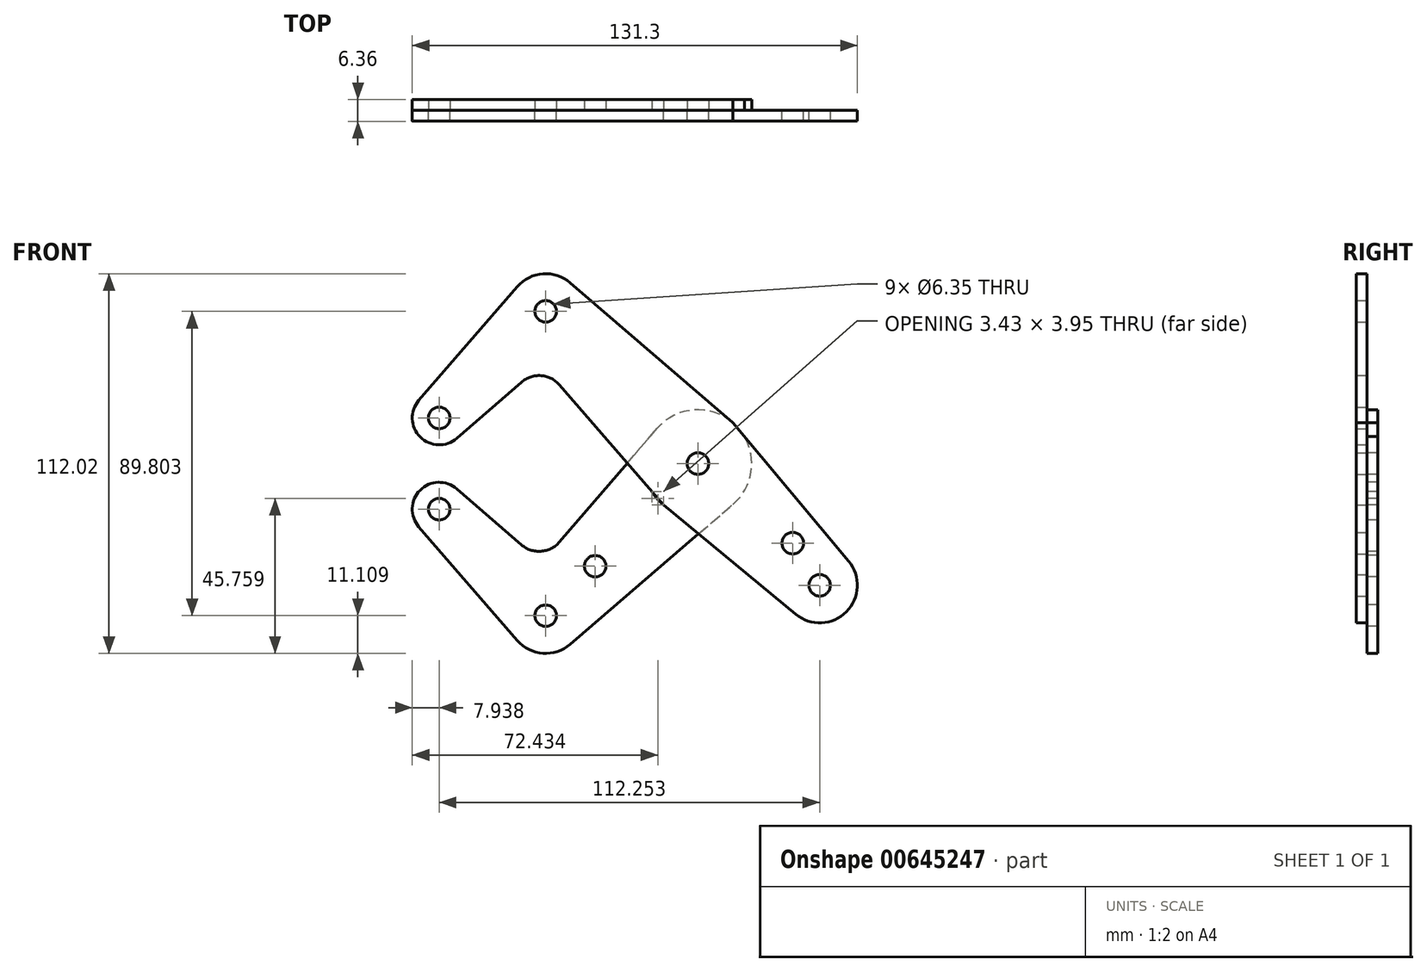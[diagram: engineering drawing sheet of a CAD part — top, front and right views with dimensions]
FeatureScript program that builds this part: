
annotation { "Feature Type Name" : "Feature", "Feature Type Description" : "" }
export const myFeature = defineFeature(function(context is Context, id is Id, definition is map)
    precondition{}
    {
        {
            var Q0;
            Q0=qCreatedBy(makeId("Front.planeOp"),FACE);
            var sketch = newSketch(context, id + "F0", { "sketchPlane" : qUnion([Q0])});
            skLineSegment(sketch, "E0", {"start": v(-76.33, 13.47) * mm, "end": v(-44.9, 44.9) * mm, "construction": true});
            skLineSegment(sketch, "E1", {"start": v(-44.9, 44.9) * mm, "end": v(35.92, -35.92) * mm, "construction": true});
            skCircle(sketch, "E2", {"center": v(-76.33, 13.47) * mm, "radius": 3.18 * mm});
            skCircle(sketch, "E3", {"center": v(-76.33, 13.47) * mm, "radius": 7.94 * mm});
            skCircle(sketch, "E4", {"center": v(-44.9, 44.9) * mm, "radius": 11.11 * mm});
            skCircle(sketch, "E5", {"center": v(-44.9, 44.9) * mm, "radius": 3.18 * mm});
            skPoint(sketch, "E6", {"position": v(0, 0) * mm});
            skCircle(sketch, "E7", {"center": v(0, 0) * mm, "radius": 3.98 * mm});
            skCircle(sketch, "E8", {"center": v(0, 0) * mm, "radius": 3.18 * mm});
            skCircle(sketch, "E9", {"center": v(0, 0) * mm, "radius": 15.88 * mm});
            skCircle(sketch, "E10", {"center": v(35.92, -35.92) * mm, "radius": 3.18 * mm});
            skCircle(sketch, "E11", {"center": v(35.92, -35.92) * mm, "radius": 11.11 * mm});
            skCircle(sketch, "E12", {"center": v(27.97, -23.48) * mm, "radius": 3.18 * mm});
            skLineSegment(sketch, "E13", {"start": v(-82.33, 18.67) * mm, "end": v(-53.3, 52.18) * mm});
            skLineSegment(sketch, "E14", {"start": v(-37.66, 53.33) * mm, "end": v(10.35, 12.04) * mm});
            skLineSegment(sketch, "E15", {"start": v(44.45, -28.8) * mm, "end": v(10.35, 12.04) * mm});
            skLineSegment(sketch, "E16", {"start": v(28.83, -44.48) * mm, "end": v(-10.12, -12.23) * mm});
            skLineSegment(sketch, "E17", {"start": v(-71.13, 7.47) * mm, "end": v(-52.03, 24.02) * mm});
            skLineSegment(sketch, "E18", {"start": v(-10.12, -12.23) * mm, "end": v(-40.82, 23.21) * mm});
            skArc(sketch, "E19.filletArc", {"start": v(-40.82, 23.21) * mm, "mid": v(-46.26, 25.94) * mm, "end": v(-52.03, 24.02) * mm});
            skLineSegment(sketch, "E20", {"start": v(0, 0) * mm, "end": v(-44.9, -44.9) * mm, "construction": true});
            skLineSegment(sketch, "E21", {"start": v(-44.9, -44.9) * mm, "end": v(-76.33, -13.47) * mm, "construction": true});
            skCircle(sketch, "E22", {"center": v(-76.33, -13.47) * mm, "radius": 7.94 * mm});
            skCircle(sketch, "E23", {"center": v(-76.33, -13.47) * mm, "radius": 3.18 * mm});
            skCircle(sketch, "E24", {"center": v(-44.9, -44.9) * mm, "radius": 11.11 * mm});
            skCircle(sketch, "E25", {"center": v(-44.9, -44.9) * mm, "radius": 3.18 * mm});
            skCircle(sketch, "E26", {"center": v(-30.3, -30.3) * mm, "radius": 3.18 * mm});
            skLineSegment(sketch, "E27", {"start": v(-71.13, -7.47) * mm, "end": v(-52.08, -23.98) * mm});
            skLineSegment(sketch, "E28", {"start": v(-82.33, -18.67) * mm, "end": v(-53.3, -52.18) * mm});
            skLineSegment(sketch, "E29", {"start": v(-40.85, -23.15) * mm, "end": v(-11.26, 11.26) * mm});
            skLineSegment(sketch, "E30", {"start": v(-37.66, -53.33) * mm, "end": v(11.26, -11.26) * mm});
            skArc(sketch, "E31.filletArc", {"start": v(-52.08, -23.98) * mm, "mid": v(-46.3, -25.9) * mm, "end": v(-40.85, -23.15) * mm});
            skSolve(sketch);
        }
        {
            var Q0;
            Q0=makeQuery(id+"F0.imprint","IMPRINT",FACE,{"disambiguationData":[TD([[makeQuery(id+"F0.imprint","IMPRINT",EDGE,{"derivedFrom":sQuery(id+"F0.wireOp",EDGE,"E2")}),-1.0]])]});
            var Q1;
            {var subQ0=sQuery(id+"F0.wireOp",EDGE,"E13");Q1=makeQuery(id+"F0.imprint","IMPRINT",FACE,{"disambiguationData":[TD([[makeQuery(id+"F0.imprint","IMPRINT",EDGE,{"derivedFrom":subQ0}),-1.0]])]});}
            var Q2;
            Q2=makeQuery(id+"F0.imprint","IMPRINT",FACE,{"disambiguationData":[TD([[makeQuery(id+"F0.imprint","IMPRINT",EDGE,{"derivedFrom":sQuery(id+"F0.wireOp",EDGE,"E5")}),-1.0]])]});
            var Q3;
            Q3=makeQuery(id+"F0.imprint","IMPRINT",FACE,{"disambiguationData":[TD([[makeQuery(id+"F0.imprint","IMPRINT",EDGE,{"derivedFrom":sQuery(id+"F0.wireOp",EDGE,"E7")}),-1.0]])]});
            var Q4;
            Q4=makeQuery(id+"F0.imprint","IMPRINT",FACE,{"disambiguationData":[TD([[makeQuery(id+"F0.imprint","IMPRINT",EDGE,{"derivedFrom":sQuery(id+"F0.wireOp",EDGE,"E12")}),-1.0]])]});
            var Q5;
            Q5=makeQuery(id+"F0.imprint","IMPRINT",FACE,{"disambiguationData":[TD([[makeQuery(id+"F0.imprint","IMPRINT",EDGE,{"derivedFrom":sQuery(id+"F0.wireOp",EDGE,"E10")}),-1.0]])]});
            var Q6;
            Q6=makeQuery(id+"F0.imprint","IMPRINT",FACE,{"disambiguationData":[TD([[makeQuery(id+"F0.imprint","IMPRINT",EDGE,{"derivedFrom":sQuery(id+"F0.wireOp",EDGE,"E7")}),1.0]])]});
            var Q7;
            {var subQ0=sQuery(id+"F0.wireOp",EDGE,"E29");var subQ1=sQuery(id+"F0.wireOp",EDGE,"E9");var subQ2=makeQuery(id+"F0.imprint","INTERSECT",VERTEX,{"derivedFrom":[subQ1,subQ0]});Q7=makeQuery(id+"F0.imprint","IMPRINT",FACE,{"disambiguationData":[TD([[makeQuery(id+"F0.imprint","IMPRINT",EDGE,{"disambiguationData":[TD([[subQ2,-1.0]])],"derivedFrom":subQ1}),-1.0]])]});}
            var Q8;
            {var subQ1=sQuery(id+"F0.wireOp",EDGE,"E9");var subQ3=sQuery(id+"F0.wireOp",EDGE,"E30");var subQ4=makeQuery(id+"F0.imprint","INTERSECT",VERTEX,{"derivedFrom":[subQ1,subQ3]});Q8=makeQuery(id+"F0.imprint","IMPRINT",FACE,{"disambiguationData":[TD([[makeQuery(id+"F0.imprint","IMPRINT",EDGE,{"disambiguationData":[TD([[subQ4,1.0]])],"derivedFrom":subQ3}),1.0]])]});}
            extrude(context, id + "F1", {"entities" : qUnion([Q0, Q1, Q2, Q3, Q4, Q5, Q6, Q7, Q8]), "depth" : 3.17 * mm, "offsetDistance" : 25.4 * mm});
        }
        {
            var Q0;
            Q0=makeQuery(id+"F0.imprint","IMPRINT",FACE,{"disambiguationData":[TD([[makeQuery(id+"F0.imprint","IMPRINT",EDGE,{"derivedFrom":sQuery(id+"F0.wireOp",EDGE,"E23")}),-1.0]])]});
            var Q1;
            Q1=makeQuery(id+"F0.imprint","IMPRINT",FACE,{"disambiguationData":[TD([[makeQuery(id+"F0.imprint","IMPRINT",EDGE,{"derivedFrom":sQuery(id+"F0.wireOp",EDGE,"E26")}),-1.0]])]});
            var Q2;
            Q2=makeQuery(id+"F0.imprint","IMPRINT",FACE,{"disambiguationData":[TD([[makeQuery(id+"F0.imprint","IMPRINT",EDGE,{"derivedFrom":sQuery(id+"F0.wireOp",EDGE,"E25")}),-1.0]])]});
            var Q3;
            {var subQ0=sQuery(id+"F0.wireOp",EDGE,"E29");var subQ1=sQuery(id+"F0.wireOp",EDGE,"E9");var subQ2=makeQuery(id+"F0.imprint","INTERSECT",VERTEX,{"derivedFrom":[subQ1,subQ0]});Q3=makeQuery(id+"F0.imprint","IMPRINT",FACE,{"disambiguationData":[TD([[makeQuery(id+"F0.imprint","IMPRINT",EDGE,{"disambiguationData":[TD([[subQ2,-1.0]])],"derivedFrom":subQ1}),-1.0]])]});}
            var Q4;
            {var subQ1=sQuery(id+"F0.wireOp",EDGE,"E9");var subQ3=sQuery(id+"F0.wireOp",EDGE,"E30");var subQ4=makeQuery(id+"F0.imprint","INTERSECT",VERTEX,{"derivedFrom":[subQ1,subQ3]});Q4=makeQuery(id+"F0.imprint","IMPRINT",FACE,{"disambiguationData":[TD([[makeQuery(id+"F0.imprint","IMPRINT",EDGE,{"disambiguationData":[TD([[subQ4,1.0]])],"derivedFrom":subQ3}),1.0]])]});}
            var Q5;
            Q5=makeQuery(id+"F0.imprint","IMPRINT",FACE,{"disambiguationData":[TD([[makeQuery(id+"F0.imprint","IMPRINT",EDGE,{"derivedFrom":sQuery(id+"F0.wireOp",EDGE,"E7")}),-1.0]])]});
            var Q6;
            Q6=makeQuery(id+"F0.imprint","IMPRINT",FACE,{"disambiguationData":[TD([[makeQuery(id+"F0.imprint","IMPRINT",EDGE,{"derivedFrom":sQuery(id+"F0.wireOp",EDGE,"E7")}),1.0]])]});
            extrude(context, id + "F2", {"entities" : qUnion([Q0, Q1, Q2, Q3, Q4, Q5, Q6]), "oppositeDirection" : true, "depth" : 3.17 * mm, "offsetDistance" : 25.4 * mm});
        }
    });
